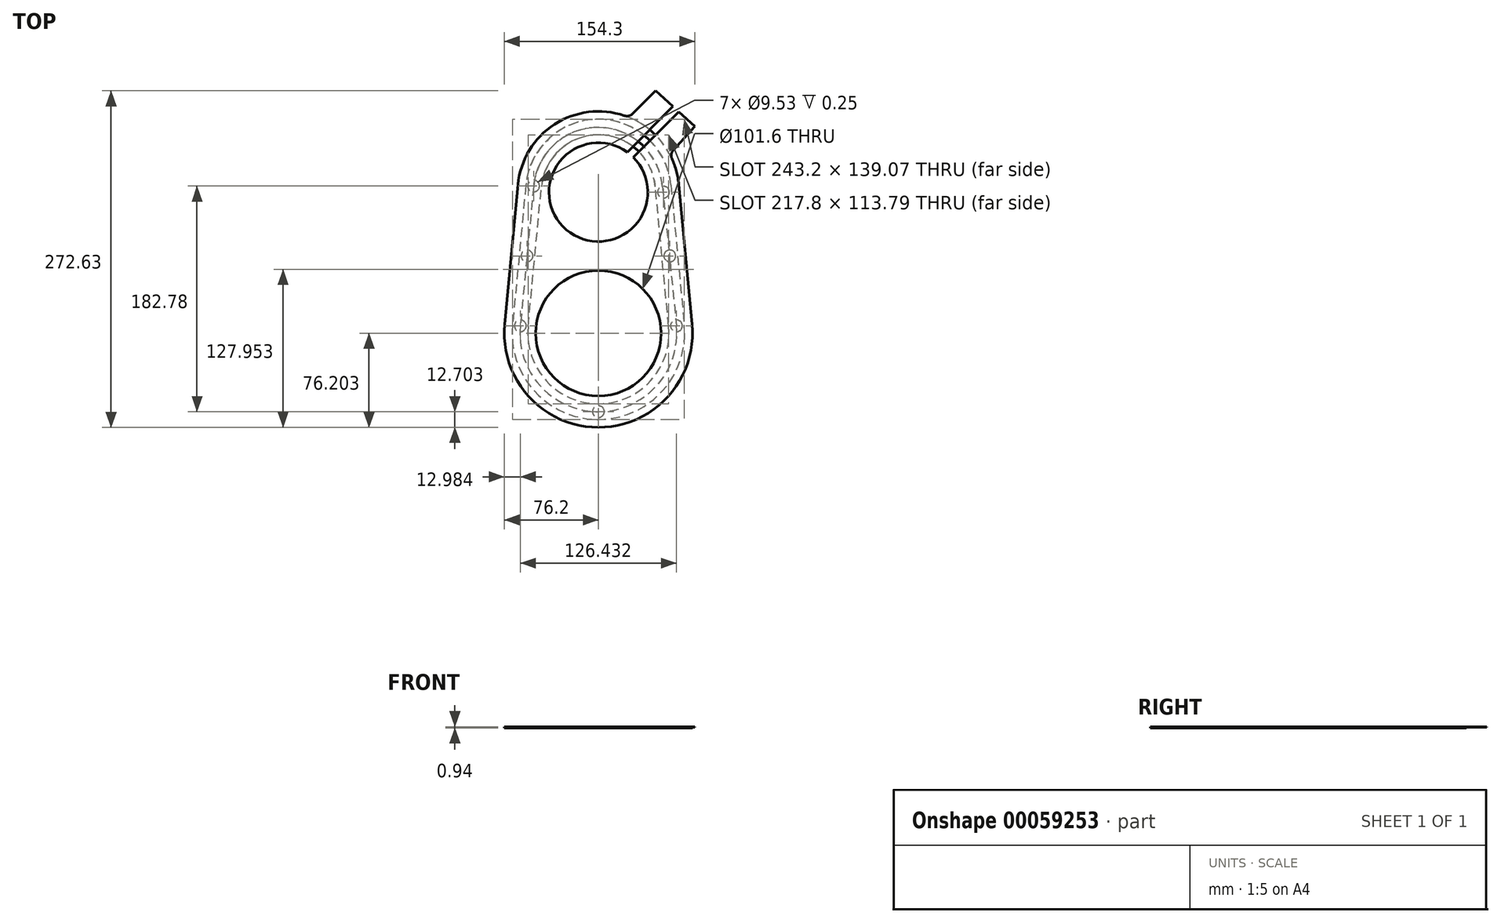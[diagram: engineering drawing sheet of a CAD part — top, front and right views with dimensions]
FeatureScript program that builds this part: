
annotation { "Feature Type Name" : "Feature", "Feature Type Description" : "" }
export const myFeature = defineFeature(function(context is Context, id is Id, definition is map)
    precondition{}
    {
        {
            assignVariable(context, id + "F0", {"name" : "matthickness", "anyValue" : .472});
        }
        {
            assignVariable(context, id + "F1", {"name" : "brushdepth", "anyValue" : .25});
        }
        {
            assignVariable(context, id + "F2", {"name" : "magdepth", "anyValue" : .25});
        }
        {
            var Q0;
            Q0=qCreatedBy(makeId("Top.planeOp"),FACE);
            var sketch = newSketch(context, id + "F3", { "sketchPlane" : qUnion([Q0])});
            skArc(sketch, "E0", {"start": v(23.44, 68.99) * mm, "mid": v(-25.94, 6.13) * mm, "end": v(28.28, 64.86) * mm});
            skCircle(sketch, "E1", {"center": v(0, -77.73) * mm, "radius": 50.8 * mm});
            skArc(sketch, "E2", {"start": v(65.1, 42.75) * mm, "mid": v(63.19, 53.44) * mm, "end": v(59.53, 63.66) * mm});
            skArc(sketch, "E3", {"start": v(-75.86, -70.53) * mm, "mid": v(0, -153.93) * mm, "end": v(75.86, -70.53) * mm});
            skLineSegment(sketch, "E4", {"start": v(-65.1, 42.75) * mm, "end": v(-75.86, -70.53) * mm});
            skLineSegment(sketch, "E5", {"start": v(65.1, 42.75) * mm, "end": v(75.86, -70.53) * mm});
            skLineSegment(sketch, "E6", {"start": v(0, 36.57) * mm, "end": v(130.77, 36.57) * mm, "construction": true});
            skLineSegment(sketch, "E7", {"start": v(0, 36.57) * mm, "end": v(82.7, 119.27) * mm, "construction": true});
            skLineSegment(sketch, "E8.0", {"start": v(-4.92, 40.63) * mm, "end": v(78.2, 123.76) * mm, "construction": true});
            skLineSegment(sketch, "E9.0", {"start": v(15.43, 20.36) * mm, "end": v(94.07, 107.74) * mm, "construction": true});
            skLineSegment(sketch, "E10.0", {"start": v(-18.39, 54.1) * mm, "end": v(64.73, 137.23) * mm, "construction": true});
            skLineSegment(sketch, "E11", {"start": v(60.59, 70.54) * mm, "end": v(78.1, 90) * mm});
            skLineSegment(sketch, "E12", {"start": v(78.1, 90) * mm, "end": v(65.11, 101.69) * mm});
            skLineSegment(sketch, "E13", {"start": v(65.11, 101.69) * mm, "end": v(28.28, 64.86) * mm});
            skLineSegment(sketch, "E14", {"start": v(23.44, 68.99) * mm, "end": v(60.39, 105.94) * mm});
            skLineSegment(sketch, "E15", {"start": v(60.39, 105.94) * mm, "end": v(46.2, 118.7) * mm});
            skLineSegment(sketch, "E16", {"start": v(46.2, 118.7) * mm, "end": v(27.54, 100.03) * mm});
            skLineSegment(sketch, "E17", {"start": v(46.2, 118.7) * mm, "end": v(78.1, 90) * mm, "construction": true});
            skArc(sketch, "E18.trimOffspring", {"start": v(21, 98.5) * mm, "mid": v(-35.54, 91.47) * mm, "end": v(-65.1, 42.75) * mm});
            skPoint(sketch, "E19.visualSharp", {"position": v(24.65, 97.15) * mm});
            skArc(sketch, "E19.filletArc", {"start": v(21, 98.5) * mm, "mid": v(24.49, 98.34) * mm, "end": v(27.54, 100.03) * mm});
            skPoint(sketch, "E20.visualSharp", {"position": v(57.7, 67.34) * mm});
            skArc(sketch, "E20.filletArc", {"start": v(60.59, 70.54) * mm, "mid": v(59.03, 67.26) * mm, "end": v(59.53, 63.66) * mm});
            skArc(sketch, "E21.0", {"start": v(30.88, 79.28) * mm, "mid": v(-21.73, 84.58) * mm, "end": v(-52.46, 41.55) * mm, "construction": true});
            skArc(sketch, "E22.0", {"start": v(-63.22, -71.73) * mm, "mid": v(0, -141.23) * mm, "end": v(63.22, -71.73) * mm, "construction": true});
            skLineSegment(sketch, "E23", {"start": v(-63.22, -71.73) * mm, "end": v(-52.46, 41.55) * mm, "construction": true});
            skLineSegment(sketch, "E24", {"start": v(63.22, -71.73) * mm, "end": v(52.46, 41.55) * mm, "construction": true});
            skArc(sketch, "E25.trimOffspring", {"start": v(52.7, 36.57) * mm, "mid": v(48.69, 56.74) * mm, "end": v(37.26, 73.84) * mm, "construction": true});
            skCircle(sketch, "E26", {"center": v(-52.46, 41.55) * mm, "radius": 4.76 * mm});
            skCircle(sketch, "E27", {"center": v(52.7, 36.57) * mm, "radius": 4.76 * mm});
            skCircle(sketch, "E28", {"center": v(-63.22, -71.73) * mm, "radius": 4.76 * mm});
            skCircle(sketch, "E29", {"center": v(63.22, -71.73) * mm, "radius": 4.76 * mm});
            skCircle(sketch, "E30", {"center": v(0, -141.23) * mm, "radius": 4.76 * mm});
            skLineSegment(sketch, "E31", {"start": v(-97.32, -15.09) * mm, "end": v(96.6, -15.09) * mm, "construction": true});
            skPoint(sketch, "E31.startSnap0", {"position": v(-57.84, -15.09) * mm});
            skPoint(sketch, "E31.endSnap0", {"position": v(57.84, -15.09) * mm});
            skCircle(sketch, "E32", {"center": v(-57.84, -15.09) * mm, "radius": 4.76 * mm});
            skCircle(sketch, "E33", {"center": v(57.84, -15.09) * mm, "radius": 4.76 * mm});
            skSolve(sketch);
        }
        {
            var Q0;
            Q0=makeQuery(id+"F3.imprint","IMPRINT",FACE,{"disambiguationData":[TD([[makeQuery(id+"F3.imprint","IMPRINT",EDGE,{"derivedFrom":sQuery(id+"F3.wireOp",EDGE,"E0")}),-1.0]])]});
            var Q1;
            Q1=makeQuery(id+"F3.imprint","IMPRINT",FACE,{"disambiguationData":[TD([[makeQuery(id+"F3.imprint","IMPRINT",EDGE,{"derivedFrom":sQuery(id+"F3.wireOp",EDGE,"E26")}),1.0]])]});
            var Q2;
            Q2=makeQuery(id+"F3.imprint","IMPRINT",FACE,{"disambiguationData":[TD([[makeQuery(id+"F3.imprint","IMPRINT",EDGE,{"derivedFrom":sQuery(id+"F3.wireOp",EDGE,"E27")}),1.0]])]});
            var Q3;
            Q3=makeQuery(id+"F3.imprint","IMPRINT",FACE,{"disambiguationData":[TD([[makeQuery(id+"F3.imprint","IMPRINT",EDGE,{"derivedFrom":sQuery(id+"F3.wireOp",EDGE,"E33")}),1.0]])]});
            var Q4;
            Q4=makeQuery(id+"F3.imprint","IMPRINT",FACE,{"disambiguationData":[TD([[makeQuery(id+"F3.imprint","IMPRINT",EDGE,{"derivedFrom":sQuery(id+"F3.wireOp",EDGE,"E29")}),1.0]])]});
            var Q5;
            Q5=makeQuery(id+"F3.imprint","IMPRINT",FACE,{"disambiguationData":[TD([[makeQuery(id+"F3.imprint","IMPRINT",EDGE,{"derivedFrom":sQuery(id+"F3.wireOp",EDGE,"E30")}),1.0]])]});
            var Q6;
            Q6=makeQuery(id+"F3.imprint","IMPRINT",FACE,{"disambiguationData":[TD([[makeQuery(id+"F3.imprint","IMPRINT",EDGE,{"derivedFrom":sQuery(id+"F3.wireOp",EDGE,"E28")}),1.0]])]});
            var Q7;
            Q7=makeQuery(id+"F3.imprint","IMPRINT",FACE,{"disambiguationData":[TD([[makeQuery(id+"F3.imprint","IMPRINT",EDGE,{"derivedFrom":sQuery(id+"F3.wireOp",EDGE,"E32")}),1.0]])]});
            extrude(context, id + "F4", {"entities" : qUnion([Q0, Q1, Q2, Q3, Q4, Q5, Q6, Q7]), "depth" : (getVariable(context, 'matthickness')) * mm});
        }
        {
            var Q0;
            Q0=makeQuery(id+"F4.opExtrude","SWEPT_FACE",FACE,{"disambiguationData":[OSD([sQuery(id+"F3.wireOp",EDGE,"E11")])]});
            var sketch = newSketch(context, id + "F5", { "sketchPlane" : qUnion([Q0])});
            skCircle(sketch, "E34", {"center": v(106.05, 6) * mm, "radius": 3.18 * mm});
            skPoint(sketch, "E34.centerSnap0", {"position": v(119.14, 6) * mm});
            skPoint(sketch, "E34.centerSnap1", {"position": v(106.05, 11.99) * mm});
            skSolve(sketch);
        }
        {
            var Q0;
            Q0=makeQuery(id+"F5.imprint","IMPRINT",FACE,{"disambiguationData":[TD([[makeQuery(id+"F5.imprint","IMPRINT",EDGE,{"derivedFrom":sQuery(id+"F5.wireOp",EDGE,"E34")}),1.0]])]});
            extrude(context, id + "F6", {"entities" : qUnion([Q0]), "operationType" : NewBodyOperationType.REMOVE, "endBound" : BoundingType.THROUGH_ALL, "oppositeDirection" : true, "depth" : 25.4 * mm});
        }
        {
            var Q0;
            Q0=qCreatedBy(makeId("Top.planeOp"),FACE);
            var sketch = newSketch(context, id + "F7", { "sketchPlane" : qUnion([Q0])});
            skPoint(sketch, "E35.0", {"position": v(-75.86, -70.53) * mm});
            skPoint(sketch, "E36.0", {"position": v(-65.1, 42.75) * mm});
            skArc(sketch, "E37", {"start": v(-75.86, -70.53) * mm, "mid": v(0, -153.93) * mm, "end": v(75.86, -70.53) * mm});
            skArc(sketch, "E38", {"start": v(65.1, 42.75) * mm, "mid": v(0, 101.97) * mm, "end": v(-65.1, 42.75) * mm});
            skLineSegment(sketch, "E39", {"start": v(-75.86, -70.53) * mm, "end": v(-65.1, 42.75) * mm});
            skLineSegment(sketch, "E40", {"start": v(75.86, -70.53) * mm, "end": v(65.1, 42.75) * mm});
            skLineSegment(sketch, "E41.0", {"start": v(-56.9, -72.33) * mm, "end": v(-46.14, 40.95) * mm});
            skArc(sketch, "E41.1", {"start": v(-56.9, -72.33) * mm, "mid": v(0, -134.88) * mm, "end": v(56.9, -72.33) * mm});
            skLineSegment(sketch, "E41.2", {"start": v(56.9, -72.33) * mm, "end": v(46.14, 40.95) * mm});
            skArc(sketch, "E41.3", {"start": v(46.14, 40.95) * mm, "mid": v(0, 82.92) * mm, "end": v(-46.14, 40.95) * mm});
            skArc(sketch, "E42", {"start": v(-63.22, -71.72) * mm, "mid": v(0.17, -141.23) * mm, "end": v(63.18, -71.39) * mm});
            skArc(sketch, "E43", {"start": v(-69.54, -71.13) * mm, "mid": v(0, -147.58) * mm, "end": v(69.54, -71.13) * mm});
            skLineSegment(sketch, "E44", {"start": v(51.87, 41.3) * mm, "end": v(63.18, -71.39) * mm});
            skLineSegment(sketch, "E45", {"start": v(58.79, 42.15) * mm, "end": v(69.54, -71.13) * mm});
            skLineSegment(sketch, "E46", {"start": v(-52.5, 41.18) * mm, "end": v(-63.22, -71.72) * mm});
            skLineSegment(sketch, "E47", {"start": v(-58.79, 42.15) * mm, "end": v(-69.54, -71.13) * mm});
            skArc(sketch, "E48.trimOffspring", {"start": v(51.87, 41.3) * mm, "mid": v(-0.36, 88.94) * mm, "end": v(-52.5, 41.18) * mm});
            skArc(sketch, "E49.trimOffspring", {"start": v(58.79, 42.15) * mm, "mid": v(0, 95.62) * mm, "end": v(-58.79, 42.15) * mm});
            skCircle(sketch, "E50.0", {"center": v(63.22, -71.73) * mm, "radius": 4.76 * mm});
            skCircle(sketch, "E51.0", {"center": v(57.84, -15.09) * mm, "radius": 4.76 * mm});
            skCircle(sketch, "E52.0", {"center": v(52.7, 36.57) * mm, "radius": 4.76 * mm});
            skCircle(sketch, "E53.0", {"center": v(-52.46, 41.55) * mm, "radius": 4.76 * mm});
            skCircle(sketch, "E54.0", {"center": v(-57.84, -15.09) * mm, "radius": 4.76 * mm});
            skCircle(sketch, "E55.0", {"center": v(-63.22, -71.73) * mm, "radius": 4.76 * mm});
            skCircle(sketch, "E56.0", {"center": v(0, -141.23) * mm, "radius": 4.76 * mm});
            skSolve(sketch);
        }
        {
            var Q0;
            Q0=makeQuery(id+"F7.imprint","IMPRINT",FACE,{"disambiguationData":[TD([[makeQuery(id+"F7.imprint","IMPRINT",EDGE,{"derivedFrom":sQuery(id+"F7.wireOp",EDGE,"E37")}),1.0]])]});
            var Q1;
            Q1=makeQuery(id+"F7.imprint","IMPRINT",FACE,{"disambiguationData":[TD([[makeQuery(id+"F7.imprint","IMPRINT",EDGE,{"derivedFrom":sQuery(id+"F7.wireOp",EDGE,"E43")}),1.0]])]});
            var Q2;
            Q2=makeQuery(id+"F7.imprint","IMPRINT",FACE,{"disambiguationData":[TD([[makeQuery(id+"F7.imprint","IMPRINT",EDGE,{"derivedFrom":sQuery(id+"F7.wireOp",EDGE,"E41.0")}),1.0]])]});
            var Q3;
            {var subQ0=sQuery(id+"F7.wireOp",EDGE,"E51.0");var subQ1=sQuery(id+"F7.wireOp",EDGE,"E44");var subQ2=makeQuery(id+"F7.imprint","INTERSECT",VERTEX,{"disambiguationData":[OD(0.0)],"derivedFrom":[subQ1,subQ0]});Q3=makeQuery(id+"F7.imprint","IMPRINT",FACE,{"disambiguationData":[TD([[makeQuery(id+"F7.imprint","IMPRINT",EDGE,{"disambiguationData":[TD([[subQ2,-1.0]])],"derivedFrom":subQ1}),-1.0]])]});}
            var Q4;
            {var subQ0=sQuery(id+"F7.wireOp",EDGE,"E51.0");var subQ1=sQuery(id+"F7.wireOp",EDGE,"E44");var subQ2=makeQuery(id+"F7.imprint","INTERSECT",VERTEX,{"disambiguationData":[OD(0.0)],"derivedFrom":[subQ1,subQ0]});Q4=makeQuery(id+"F7.imprint","IMPRINT",FACE,{"disambiguationData":[TD([[makeQuery(id+"F7.imprint","IMPRINT",EDGE,{"disambiguationData":[TD([[subQ2,-1.0]])],"derivedFrom":subQ1}),1.0]])]});}
            var Q5;
            {var subQ0=sQuery(id+"F7.wireOp",EDGE,"E44");var subQ1=sQuery(id+"F7.wireOp",EDGE,"E42");var subQ2=makeQuery(id+"F7.imprint","INTERSECT",VERTEX,{"derivedFrom":[subQ1,subQ0]});Q5=makeQuery(id+"F7.imprint","IMPRINT",FACE,{"disambiguationData":[TD([[makeQuery(id+"F7.imprint","IMPRINT",EDGE,{"disambiguationData":[TD([[subQ2,1.0]])],"derivedFrom":subQ1}),-1.0]])]});}
            var Q6;
            {var subQ0=sQuery(id+"F7.wireOp",EDGE,"E44");var subQ1=sQuery(id+"F7.wireOp",EDGE,"E42");var subQ2=makeQuery(id+"F7.imprint","INTERSECT",VERTEX,{"derivedFrom":[subQ1,subQ0]});Q6=makeQuery(id+"F7.imprint","IMPRINT",FACE,{"disambiguationData":[TD([[makeQuery(id+"F7.imprint","IMPRINT",EDGE,{"disambiguationData":[TD([[subQ2,1.0]])],"derivedFrom":subQ1}),1.0]])]});}
            var Q7;
            {var subQ0=sQuery(id+"F7.wireOp",EDGE,"E56.0");var subQ1=sQuery(id+"F7.wireOp",EDGE,"E42");var subQ2=makeQuery(id+"F7.imprint","INTERSECT",VERTEX,{"disambiguationData":[OD(0.0)],"derivedFrom":[subQ1,subQ0]});Q7=makeQuery(id+"F7.imprint","IMPRINT",FACE,{"disambiguationData":[TD([[makeQuery(id+"F7.imprint","IMPRINT",EDGE,{"disambiguationData":[TD([[subQ2,-1.0]])],"derivedFrom":subQ1}),1.0]])]});}
            var Q8;
            {var subQ0=sQuery(id+"F7.wireOp",EDGE,"E56.0");var subQ1=sQuery(id+"F7.wireOp",EDGE,"E42");var subQ2=makeQuery(id+"F7.imprint","INTERSECT",VERTEX,{"disambiguationData":[OD(0.0)],"derivedFrom":[subQ1,subQ0]});Q8=makeQuery(id+"F7.imprint","IMPRINT",FACE,{"disambiguationData":[TD([[makeQuery(id+"F7.imprint","IMPRINT",EDGE,{"disambiguationData":[TD([[subQ2,-1.0]])],"derivedFrom":subQ1}),-1.0]])]});}
            var Q9;
            {var subQ0=sQuery(id+"F7.wireOp",EDGE,"E46");var subQ1=sQuery(id+"F7.wireOp",EDGE,"E42");var subQ2=makeQuery(id+"F7.imprint","INTERSECT",VERTEX,{"derivedFrom":[subQ1,subQ0]});Q9=makeQuery(id+"F7.imprint","IMPRINT",FACE,{"disambiguationData":[TD([[makeQuery(id+"F7.imprint","IMPRINT",EDGE,{"disambiguationData":[TD([[subQ2,-1.0]])],"derivedFrom":subQ1}),1.0]])]});}
            var Q10;
            {var subQ0=sQuery(id+"F7.wireOp",EDGE,"E46");var subQ1=sQuery(id+"F7.wireOp",EDGE,"E42");var subQ2=makeQuery(id+"F7.imprint","INTERSECT",VERTEX,{"derivedFrom":[subQ1,subQ0]});Q10=makeQuery(id+"F7.imprint","IMPRINT",FACE,{"disambiguationData":[TD([[makeQuery(id+"F7.imprint","IMPRINT",EDGE,{"disambiguationData":[TD([[subQ2,-1.0]])],"derivedFrom":subQ1}),-1.0]])]});}
            var Q11;
            {var subQ0=sQuery(id+"F7.wireOp",EDGE,"E54.0");var subQ1=sQuery(id+"F7.wireOp",EDGE,"E46");var subQ2=makeQuery(id+"F7.imprint","INTERSECT",VERTEX,{"disambiguationData":[OD(0.0)],"derivedFrom":[subQ1,subQ0]});Q11=makeQuery(id+"F7.imprint","IMPRINT",FACE,{"disambiguationData":[TD([[makeQuery(id+"F7.imprint","IMPRINT",EDGE,{"disambiguationData":[TD([[subQ2,-1.0]])],"derivedFrom":subQ1}),1.0]])]});}
            var Q12;
            {var subQ0=sQuery(id+"F7.wireOp",EDGE,"E54.0");var subQ1=sQuery(id+"F7.wireOp",EDGE,"E46");var subQ2=makeQuery(id+"F7.imprint","INTERSECT",VERTEX,{"disambiguationData":[OD(0.0)],"derivedFrom":[subQ1,subQ0]});Q12=makeQuery(id+"F7.imprint","IMPRINT",FACE,{"disambiguationData":[TD([[makeQuery(id+"F7.imprint","IMPRINT",EDGE,{"disambiguationData":[TD([[subQ2,-1.0]])],"derivedFrom":subQ1}),-1.0]])]});}
            var Q13;
            {var subQ0=sQuery(id+"F7.wireOp",EDGE,"E48.trimOffspring");var subQ1=sQuery(id+"F7.wireOp",EDGE,"E46");var subQ2=makeQuery(id+"F7.imprint","INTERSECT",VERTEX,{"derivedFrom":[subQ1,subQ0]});Q13=makeQuery(id+"F7.imprint","IMPRINT",FACE,{"disambiguationData":[TD([[makeQuery(id+"F7.imprint","IMPRINT",EDGE,{"disambiguationData":[TD([[subQ2,-1.0]])],"derivedFrom":subQ1}),-1.0]])]});}
            var Q14;
            {var subQ0=sQuery(id+"F7.wireOp",EDGE,"E48.trimOffspring");var subQ1=sQuery(id+"F7.wireOp",EDGE,"E46");var subQ2=makeQuery(id+"F7.imprint","INTERSECT",VERTEX,{"derivedFrom":[subQ1,subQ0]});Q14=makeQuery(id+"F7.imprint","IMPRINT",FACE,{"disambiguationData":[TD([[makeQuery(id+"F7.imprint","IMPRINT",EDGE,{"disambiguationData":[TD([[subQ2,-1.0]])],"derivedFrom":subQ1}),1.0]])]});}
            var Q15;
            {var subQ0=sQuery(id+"F7.wireOp",EDGE,"E52.0");var subQ1=sQuery(id+"F7.wireOp",EDGE,"E44");var subQ2=makeQuery(id+"F7.imprint","INTERSECT",VERTEX,{"disambiguationData":[OD(0.0)],"derivedFrom":[subQ1,subQ0]});Q15=makeQuery(id+"F7.imprint","IMPRINT",FACE,{"disambiguationData":[TD([[makeQuery(id+"F7.imprint","IMPRINT",EDGE,{"disambiguationData":[TD([[subQ2,-1.0]])],"derivedFrom":subQ1}),1.0]])]});}
            var Q16;
            {var subQ0=sQuery(id+"F7.wireOp",EDGE,"E52.0");var subQ1=sQuery(id+"F7.wireOp",EDGE,"E44");var subQ2=makeQuery(id+"F7.imprint","INTERSECT",VERTEX,{"disambiguationData":[OD(0.0)],"derivedFrom":[subQ1,subQ0]});Q16=makeQuery(id+"F7.imprint","IMPRINT",FACE,{"disambiguationData":[TD([[makeQuery(id+"F7.imprint","IMPRINT",EDGE,{"disambiguationData":[TD([[subQ2,-1.0]])],"derivedFrom":subQ1}),-1.0]])]});}
            extrude(context, id + "F8", {"entities" : qUnion([Q0, Q1, Q2, Q3, Q4, Q5, Q6, Q7, Q8, Q9, Q10, Q11, Q12, Q13, Q14, Q15, Q16]), "oppositeDirection" : true, "depth" : (getVariable(context, 'matthickness')) * mm});
        }
        {
            var Q0;
            Q0=makeQuery(id+"F8.opExtrude","CAP_FACE",FACE,{"disambiguationData":[OSD([sQuery(id+"F7.wireOp",EDGE,"E37"),sQuery(id+"F7.wireOp",EDGE,"E38"),sQuery(id+"F7.wireOp",EDGE,"E39"),sQuery(id+"F7.wireOp",EDGE,"E40"),sQuery(id+"F7.wireOp",EDGE,"E41.0"),sQuery(id+"F7.wireOp",EDGE,"E41.1"),sQuery(id+"F7.wireOp",EDGE,"E41.2"),sQuery(id+"F7.wireOp",EDGE,"E41.3")])],"isStart":false});
            var sketch = newSketch(context, id + "F9", { "sketchPlane" : qUnion([Q0])});
            skLineSegment(sketch, "E57.0", {"start": v(-58.79, -42.15) * mm, "end": v(-69.54, 71.13) * mm});
            skArc(sketch, "E57.1", {"start": v(-69.54, 71.13) * mm, "mid": v(0, 147.58) * mm, "end": v(69.54, 71.13) * mm});
            skArc(sketch, "E57.2", {"start": v(-63.22, 71.72) * mm, "mid": v(0.17, 141.23) * mm, "end": v(63.18, 71.39) * mm});
            skLineSegment(sketch, "E57.3", {"start": v(-52.5, -41.18) * mm, "end": v(-63.22, 71.72) * mm});
            skArc(sketch, "E57.4", {"start": v(58.79, -42.15) * mm, "mid": v(0, -95.62) * mm, "end": v(-58.79, -42.15) * mm});
            skArc(sketch, "E57.5", {"start": v(51.87, -41.3) * mm, "mid": v(-0.36, -88.94) * mm, "end": v(-52.5, -41.18) * mm});
            skLineSegment(sketch, "E57.6", {"start": v(58.79, -42.15) * mm, "end": v(69.54, 71.13) * mm});
            skLineSegment(sketch, "E57.7", {"start": v(51.87, -41.3) * mm, "end": v(63.18, 71.39) * mm});
            skSolve(sketch);
        }
        {
            var Q0;
            Q0=makeQuery(id+"F3.imprint","IMPRINT",FACE,{"disambiguationData":[TD([[makeQuery(id+"F3.imprint","IMPRINT",EDGE,{"derivedFrom":sQuery(id+"F3.wireOp",EDGE,"E28")}),1.0]])]});
            var Q1;
            Q1=makeQuery(id+"F3.imprint","IMPRINT",FACE,{"disambiguationData":[TD([[makeQuery(id+"F3.imprint","IMPRINT",EDGE,{"derivedFrom":sQuery(id+"F3.wireOp",EDGE,"E30")}),1.0]])]});
            var Q2;
            Q2=makeQuery(id+"F3.imprint","IMPRINT",FACE,{"disambiguationData":[TD([[makeQuery(id+"F3.imprint","IMPRINT",EDGE,{"derivedFrom":sQuery(id+"F3.wireOp",EDGE,"E29")}),1.0]])]});
            var Q3;
            Q3=makeQuery(id+"F3.imprint","IMPRINT",FACE,{"disambiguationData":[TD([[makeQuery(id+"F3.imprint","IMPRINT",EDGE,{"derivedFrom":sQuery(id+"F3.wireOp",EDGE,"E33")}),1.0]])]});
            var Q4;
            Q4=makeQuery(id+"F3.imprint","IMPRINT",FACE,{"disambiguationData":[TD([[makeQuery(id+"F3.imprint","IMPRINT",EDGE,{"derivedFrom":sQuery(id+"F3.wireOp",EDGE,"E27")}),1.0]])]});
            var Q5;
            Q5=makeQuery(id+"F3.imprint","IMPRINT",FACE,{"disambiguationData":[TD([[makeQuery(id+"F3.imprint","IMPRINT",EDGE,{"derivedFrom":sQuery(id+"F3.wireOp",EDGE,"E32")}),1.0]])]});
            var Q6;
            Q6=makeQuery(id+"F3.imprint","IMPRINT",FACE,{"disambiguationData":[TD([[makeQuery(id+"F3.imprint","IMPRINT",EDGE,{"derivedFrom":sQuery(id+"F3.wireOp",EDGE,"E26")}),1.0]])]});
            extrude(context, id + "F10", {"entities" : qUnion([Q0, Q1, Q2, Q3, Q4, Q5, Q6]), "operationType" : NewBodyOperationType.REMOVE, "depth" : (getVariable(context, 'magdepth')) * mm});
        }
        {
            var Q0;
            Q0=makeQuery(id+"F9.imprint","IMPRINT",FACE,{"disambiguationData":[TD([[makeQuery(id+"F9.imprint","IMPRINT",EDGE,{"derivedFrom":sQuery(id+"F9.wireOp",EDGE,"E57.0")}),-1.0]])]});
            extrude(context, id + "F11", {"entities" : qUnion([Q0]), "operationType" : NewBodyOperationType.REMOVE, "oppositeDirection" : true, "depth" : (getVariable(context, 'brushdepth')) * mm});
        }
        {
            var Q0;
            {var subQ0=sQuery(id+"F7.wireOp",EDGE,"E44");var subQ1=sQuery(id+"F7.wireOp",EDGE,"E42");var subQ2=makeQuery(id+"F7.imprint","INTERSECT",VERTEX,{"derivedFrom":[subQ1,subQ0]});Q0=makeQuery(id+"F7.imprint","IMPRINT",FACE,{"disambiguationData":[TD([[makeQuery(id+"F7.imprint","IMPRINT",EDGE,{"disambiguationData":[TD([[subQ2,1.0]])],"derivedFrom":subQ1}),1.0]])]});}
            var Q1;
            {var subQ0=sQuery(id+"F7.wireOp",EDGE,"E44");var subQ1=sQuery(id+"F7.wireOp",EDGE,"E42");var subQ2=makeQuery(id+"F7.imprint","INTERSECT",VERTEX,{"derivedFrom":[subQ1,subQ0]});Q1=makeQuery(id+"F7.imprint","IMPRINT",FACE,{"disambiguationData":[TD([[makeQuery(id+"F7.imprint","IMPRINT",EDGE,{"disambiguationData":[TD([[subQ2,1.0]])],"derivedFrom":subQ1}),-1.0]])]});}
            var Q2;
            {var subQ0=sQuery(id+"F7.wireOp",EDGE,"E51.0");var subQ1=sQuery(id+"F7.wireOp",EDGE,"E44");var subQ2=makeQuery(id+"F7.imprint","INTERSECT",VERTEX,{"disambiguationData":[OD(0.0)],"derivedFrom":[subQ1,subQ0]});Q2=makeQuery(id+"F7.imprint","IMPRINT",FACE,{"disambiguationData":[TD([[makeQuery(id+"F7.imprint","IMPRINT",EDGE,{"disambiguationData":[TD([[subQ2,-1.0]])],"derivedFrom":subQ1}),-1.0]])]});}
            var Q3;
            {var subQ0=sQuery(id+"F7.wireOp",EDGE,"E51.0");var subQ1=sQuery(id+"F7.wireOp",EDGE,"E44");var subQ2=makeQuery(id+"F7.imprint","INTERSECT",VERTEX,{"disambiguationData":[OD(0.0)],"derivedFrom":[subQ1,subQ0]});Q3=makeQuery(id+"F7.imprint","IMPRINT",FACE,{"disambiguationData":[TD([[makeQuery(id+"F7.imprint","IMPRINT",EDGE,{"disambiguationData":[TD([[subQ2,-1.0]])],"derivedFrom":subQ1}),1.0]])]});}
            var Q4;
            {var subQ0=sQuery(id+"F7.wireOp",EDGE,"E52.0");var subQ1=sQuery(id+"F7.wireOp",EDGE,"E44");var subQ2=makeQuery(id+"F7.imprint","INTERSECT",VERTEX,{"disambiguationData":[OD(0.0)],"derivedFrom":[subQ1,subQ0]});Q4=makeQuery(id+"F7.imprint","IMPRINT",FACE,{"disambiguationData":[TD([[makeQuery(id+"F7.imprint","IMPRINT",EDGE,{"disambiguationData":[TD([[subQ2,-1.0]])],"derivedFrom":subQ1}),-1.0]])]});}
            var Q5;
            {var subQ0=sQuery(id+"F7.wireOp",EDGE,"E52.0");var subQ1=sQuery(id+"F7.wireOp",EDGE,"E44");var subQ2=makeQuery(id+"F7.imprint","INTERSECT",VERTEX,{"disambiguationData":[OD(0.0)],"derivedFrom":[subQ1,subQ0]});Q5=makeQuery(id+"F7.imprint","IMPRINT",FACE,{"disambiguationData":[TD([[makeQuery(id+"F7.imprint","IMPRINT",EDGE,{"disambiguationData":[TD([[subQ2,-1.0]])],"derivedFrom":subQ1}),1.0]])]});}
            var Q6;
            {var subQ0=sQuery(id+"F7.wireOp",EDGE,"E48.trimOffspring");var subQ1=sQuery(id+"F7.wireOp",EDGE,"E46");var subQ2=makeQuery(id+"F7.imprint","INTERSECT",VERTEX,{"derivedFrom":[subQ1,subQ0]});Q6=makeQuery(id+"F7.imprint","IMPRINT",FACE,{"disambiguationData":[TD([[makeQuery(id+"F7.imprint","IMPRINT",EDGE,{"disambiguationData":[TD([[subQ2,-1.0]])],"derivedFrom":subQ1}),1.0]])]});}
            var Q7;
            {var subQ0=sQuery(id+"F7.wireOp",EDGE,"E48.trimOffspring");var subQ1=sQuery(id+"F7.wireOp",EDGE,"E46");var subQ2=makeQuery(id+"F7.imprint","INTERSECT",VERTEX,{"derivedFrom":[subQ1,subQ0]});Q7=makeQuery(id+"F7.imprint","IMPRINT",FACE,{"disambiguationData":[TD([[makeQuery(id+"F7.imprint","IMPRINT",EDGE,{"disambiguationData":[TD([[subQ2,-1.0]])],"derivedFrom":subQ1}),-1.0]])]});}
            var Q8;
            {var subQ0=sQuery(id+"F7.wireOp",EDGE,"E54.0");var subQ1=sQuery(id+"F7.wireOp",EDGE,"E46");var subQ2=makeQuery(id+"F7.imprint","INTERSECT",VERTEX,{"disambiguationData":[OD(0.0)],"derivedFrom":[subQ1,subQ0]});Q8=makeQuery(id+"F7.imprint","IMPRINT",FACE,{"disambiguationData":[TD([[makeQuery(id+"F7.imprint","IMPRINT",EDGE,{"disambiguationData":[TD([[subQ2,-1.0]])],"derivedFrom":subQ1}),1.0]])]});}
            var Q9;
            {var subQ0=sQuery(id+"F7.wireOp",EDGE,"E54.0");var subQ1=sQuery(id+"F7.wireOp",EDGE,"E46");var subQ2=makeQuery(id+"F7.imprint","INTERSECT",VERTEX,{"disambiguationData":[OD(0.0)],"derivedFrom":[subQ1,subQ0]});Q9=makeQuery(id+"F7.imprint","IMPRINT",FACE,{"disambiguationData":[TD([[makeQuery(id+"F7.imprint","IMPRINT",EDGE,{"disambiguationData":[TD([[subQ2,-1.0]])],"derivedFrom":subQ1}),-1.0]])]});}
            var Q10;
            {var subQ0=sQuery(id+"F7.wireOp",EDGE,"E46");var subQ1=sQuery(id+"F7.wireOp",EDGE,"E42");var subQ2=makeQuery(id+"F7.imprint","INTERSECT",VERTEX,{"derivedFrom":[subQ1,subQ0]});Q10=makeQuery(id+"F7.imprint","IMPRINT",FACE,{"disambiguationData":[TD([[makeQuery(id+"F7.imprint","IMPRINT",EDGE,{"disambiguationData":[TD([[subQ2,-1.0]])],"derivedFrom":subQ1}),1.0]])]});}
            var Q11;
            {var subQ0=sQuery(id+"F7.wireOp",EDGE,"E46");var subQ1=sQuery(id+"F7.wireOp",EDGE,"E42");var subQ2=makeQuery(id+"F7.imprint","INTERSECT",VERTEX,{"derivedFrom":[subQ1,subQ0]});Q11=makeQuery(id+"F7.imprint","IMPRINT",FACE,{"disambiguationData":[TD([[makeQuery(id+"F7.imprint","IMPRINT",EDGE,{"disambiguationData":[TD([[subQ2,-1.0]])],"derivedFrom":subQ1}),-1.0]])]});}
            var Q12;
            {var subQ0=sQuery(id+"F7.wireOp",EDGE,"E56.0");var subQ1=sQuery(id+"F7.wireOp",EDGE,"E42");var subQ2=makeQuery(id+"F7.imprint","INTERSECT",VERTEX,{"disambiguationData":[OD(0.0)],"derivedFrom":[subQ1,subQ0]});Q12=makeQuery(id+"F7.imprint","IMPRINT",FACE,{"disambiguationData":[TD([[makeQuery(id+"F7.imprint","IMPRINT",EDGE,{"disambiguationData":[TD([[subQ2,-1.0]])],"derivedFrom":subQ1}),1.0]])]});}
            var Q13;
            {var subQ0=sQuery(id+"F7.wireOp",EDGE,"E56.0");var subQ1=sQuery(id+"F7.wireOp",EDGE,"E42");var subQ2=makeQuery(id+"F7.imprint","INTERSECT",VERTEX,{"disambiguationData":[OD(0.0)],"derivedFrom":[subQ1,subQ0]});Q13=makeQuery(id+"F7.imprint","IMPRINT",FACE,{"disambiguationData":[TD([[makeQuery(id+"F7.imprint","IMPRINT",EDGE,{"disambiguationData":[TD([[subQ2,-1.0]])],"derivedFrom":subQ1}),-1.0]])]});}
            extrude(context, id + "F12", {"entities" : qUnion([Q0, Q1, Q2, Q3, Q4, Q5, Q6, Q7, Q8, Q9, Q10, Q11, Q12, Q13]), "operationType" : NewBodyOperationType.REMOVE, "oppositeDirection" : true, "depth" : (getVariable(context, 'magdepth')) * mm});
        }
    });
